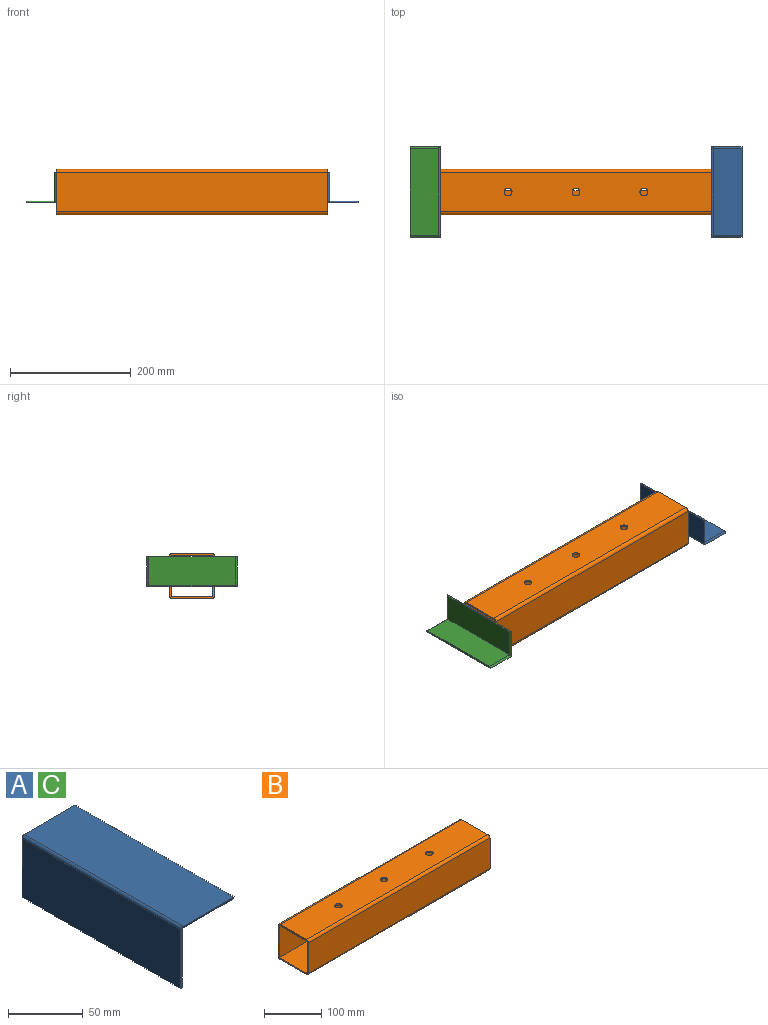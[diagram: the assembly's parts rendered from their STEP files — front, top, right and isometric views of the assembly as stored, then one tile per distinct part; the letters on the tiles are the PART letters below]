
ASSEMBLY  parts=3 mates=2
PART A: 11 faces, bbox 50x150x50 mm
  f0: plane 144x47mm, normal (0,0,-1), area 6768mm2, adj f1,f5,f8,f10
  f1: plane 150x3mm, normal (1,0,0), area 446.1mm2, adj f0,f2,f8,f10
  f2: plane 150x48mm, normal (0,0,1), area 7200mm2, adj f1,f6,f8,f10
  f3: plane 150x48mm, normal (-1,0,0), area 7200mm2, adj f4,f6,f7,f9
  f4: plane 150x3mm, normal (0,0,-1), area 446.1mm2, adj f3,f5,f7,f9
  f5: plane 144x47mm, normal (1,0,0), area 6768mm2, adj f0,f4,f7,f9
  f6: cylinder r=2mm len=150mm, axis (0,-1,0), area 471.2mm2, adj f2,f3,f7,f8,f9,f10
  f7: cylinder r=3mm len=49.41mm, axis (0,0,1), area 226.2mm2, adj f3,f4,f5,f6,f8
  f8: cylinder r=3mm len=49.41mm, axis (1,0,0), area 226.2mm2, adj f0,f1,f2,f6,f7
  f9: cylinder r=3mm len=49.41mm, axis (0,0,-1), area 226.2mm2, adj f3,f4,f5,f6,f10
  f10: cylinder r=3mm len=49.41mm, axis (-1,0,0), area 226.2mm2, adj f0,f1,f2,f6,f9
PART B: 32 faces, bbox 450x75x75 mm
  f0: plane 450x65mm, normal (0,0,-1), area 24750mm2, adj f8,f9,f10,f11,f12,f14,f15,f16
  f1: plane 450x69mm, normal (0,-1,0), area 27000mm2, adj f2,f6,f8,f9,f11,f12,f13,f15
  f2: plane 450x69mm, normal (0,0,1), area 26250mm2, adj f1,f5,f8,f9,f10,f11,f12,f14
  f3: plane 450x65mm, normal (0,1,0), area 25500mm2, adj f8,f9,f11,f12,f13,f15,f16,f17
  f4: plane 450x65mm, normal (0,0,1), area 28851.8mm2, adj f8,f9,f22,f23,f24,f29,f30
  f5: plane 450x69mm, normal (0,1,0), area 31050mm2, adj f2,f6,f8,f9
  f6: plane 450x69mm, normal (0,0,-1), area 30651.8mm2, adj f1,f5,f8,f9,f22,f23,f24
  f7: plane 450x65mm, normal (0,-1,0), area 29250mm2, adj f8,f9,f30,f31
  f8: plane 75x75mm, normal (1,0,0), area 842.5mm2, adj f0,f1,f2,f3,f4,f5,f6,f7
  f9: plane 75x75mm, normal (-1,0,0), area 842.5mm2, adj f0,f1,f2,f3,f4,f5,f6,f7
  f10: plane 50x3mm, normal (0,1,0), area 150mm2, adj f0,f2,f11,f12
  f11: plane 35x30mm, normal (1,0,0), area 180.6mm2, adj f0,f1,f2,f3,f10,f13,f27
  f12: plane 35x30mm, normal (-1,0,0), area 180.6mm2, adj f0,f1,f2,f3,f10,f13,f28
  f13: plane 50x3mm, normal (0,0,-1), area 150mm2, adj f1,f3,f11,f12
  f14: plane 50x3mm, normal (0,1,0), area 150mm2, adj f0,f2,f15,f16
  f15: plane 35x30mm, normal (1,0,0), area 180.6mm2, adj f0,f1,f2,f3,f14,f17,f26
  f16: plane 35x30mm, normal (-1,0,0), area 180.6mm2, adj f0,f1,f2,f3,f14,f17,f27
  f17: plane 50x3mm, normal (0,0,-1), area 150mm2, adj f1,f3,f15,f16
  f18: plane 50x3mm, normal (0,1,0), area 150mm2, adj f0,f2,f19,f20
  f19: plane 35x30mm, normal (1,0,0), area 180.6mm2, adj f0,f1,f2,f3,f18,f21,f25
  f20: plane 35x30mm, normal (-1,0,0), area 180.6mm2, adj f0,f1,f2,f3,f18,f21,f26
  f21: plane 50x3mm, normal (0,0,-1), area 150mm2, adj f1,f3,f19,f20
  f22: cylinder r=6.5mm len=13mm, axis (0,0,1), area 122.5mm2, adj f4,f6
  f23: cylinder r=6.5mm len=13mm, axis (0,0,1), area 122.5mm2, adj f4,f6
  f24: cylinder r=6.5mm len=13mm, axis (0,0,1), area 122.5mm2, adj f4,f6
  f25: cylinder r=5mm len=87.5mm, axis (1,0,0), area 687.2mm2, adj f0,f3,f9,f19
  f26: cylinder r=5mm len=62.5mm, axis (1,0,0), area 490.9mm2, adj f0,f3,f15,f20
  f27: cylinder r=5mm len=62.5mm, axis (1,0,0), area 490.9mm2, adj f0,f3,f11,f16
  f28: cylinder r=5mm len=87.5mm, axis (1,0,0), area 687.2mm2, adj f0,f3,f8,f12
  f29: cylinder r=5mm len=450mm, axis (-1,0,0), area 3534.3mm2, adj f3,f4,f8,f9
  f30: cylinder r=5mm len=450mm, axis (1,0,0), area 3534.3mm2, adj f4,f7,f8,f9
  f31: cylinder r=5mm len=450mm, axis (-1,0,0), area 3534.3mm2, adj f0,f7,f8,f9
PART C: same geometry as A
PLACE A rot(axis=(1,0,0),180deg) t=(532.66,-75.56,-56.94)mm
PLACE B t=(57.66,36.94,-101.44)mm fixed
PLACE C rot(axis=(0,-1,0),180deg) t=(32.66,74.44,-56.94)mm
MATE parallel A.f3 <-> B.f8  axis (-1,0,0) through (507.66,-0.56,-55.94)mm
MATE planar B.f9 <-> C.f3  axis (-1,0,0) through (57.66,-0.56,-63.94)mm
